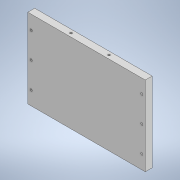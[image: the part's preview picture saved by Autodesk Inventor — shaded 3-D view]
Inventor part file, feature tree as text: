
AUTODESK INVENTOR PART (.ipt)
format: ipt  version: 2022.2 (Build 262287030, 287C)  size: 129,024 bytes
history: native  units: in
note: dims shown in document units (in); Inventor stores cm internally (conversion verified against a paired STEP export)
features: hole x3, sketch x3, extrude x1
ambient origin geometry x8: Origin, YZ Plane, XZ Plane, XY Plane, X Axis, Y Axis, Z Axis, Center Point
bodies: Solid1 (feature_tree)
feature tree (7):
  extrude  "Extrusion1"  Depth=4.5276in
  hole  "Hole1"  [1 undecoded]
  hole  "Hole2"  [1 undecoded]
  hole  "Hole3"  [1 undecoded]
  sketch  "Sketch1"  dims[d0=6.6929in d1=4.5276in]
  sketch  "Sketch3"  dims[d2=0.3937in d3=0.0in d4=0.1969in]
  sketch  "Sketch4"  dims[d5=0.7874in d11=6.2992in d14=0.125in d15=0.2953in d16=0.1476in d17=0.0984in d18=90.0deg d19=0.1969in d20=0.0in d21=0.1969in d22=0.1969in d23=1.5748in d25=2.0997in d26=0.3937in d28=0.3937in d30=0.125in d31=0.2953in d32=0.1476in d33=0.0984in d34=90.0deg d35=0.1969in d36=0.0in d46=0.125in d47=0.2953in d48=0.1476in d49=0.0984in d50=90.0deg d51=0.1969in d52=0.0in d53=1.1811in d55=1.4764in d56=0.3937in d58=0.3937in d60=1.1811in d62=1.4764in d63=0.3937in d65=0.3937in d67=0.1969in d69=1.0827in d70=0.7874in d72=2.1654in d73=0.3937in d75=0.3937in]
note: 3 required parameter values undecoded (feature->parameter linkage not recoverable at this tier; creation-order binding heuristic only, values carry confidence <= 0.55)
